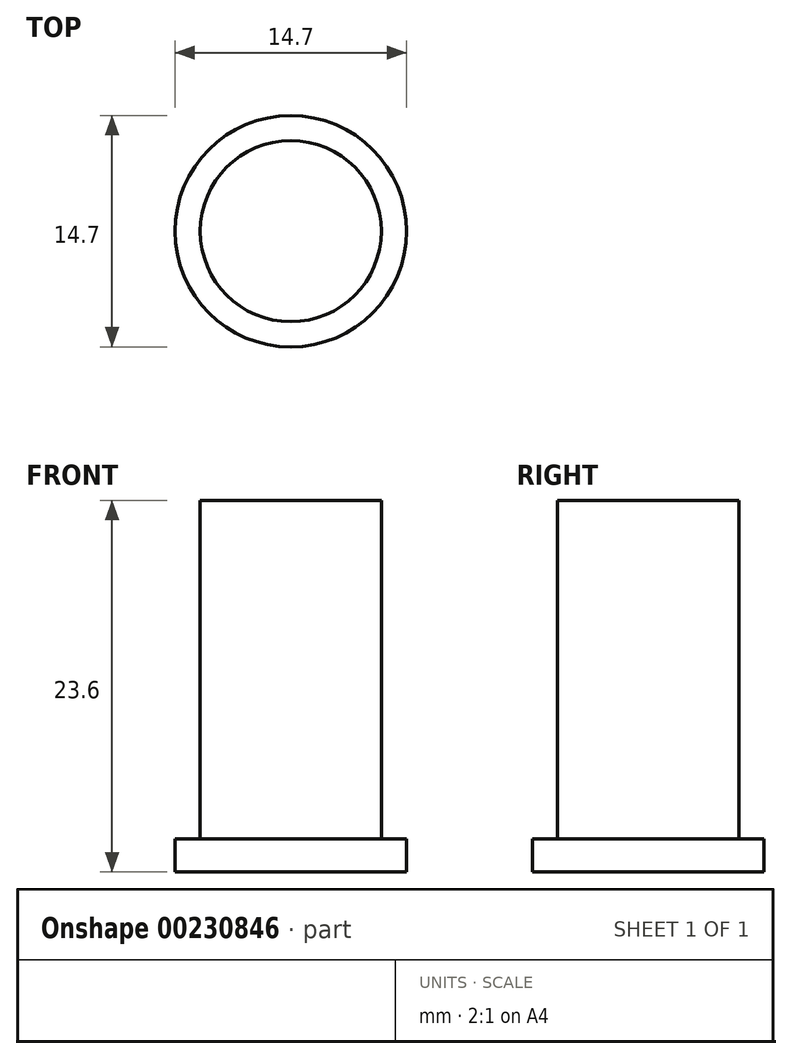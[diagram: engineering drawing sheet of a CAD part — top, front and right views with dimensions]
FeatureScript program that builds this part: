
annotation { "Feature Type Name" : "Feature", "Feature Type Description" : "" }
export const myFeature = defineFeature(function(context is Context, id is Id, definition is map)
    precondition{}
    {
        {
            var Q0;
            Q0=qCreatedBy(makeId("Top.planeOp"),FACE);
            var sketch = newSketch(context, id + "F0", { "sketchPlane" : qUnion([Q0])});
            skCircle(sketch, "E0", {"center": v(0, 0) * mm, "radius": 5.75 * mm});
            skSolve(sketch);
        }
        {
            var Q0;
            Q0=makeQuery(id+"F0.imprint","IMPRINT",FACE,{"disambiguationData":[TD([[makeQuery(id+"F0.imprint","IMPRINT",EDGE,{"derivedFrom":sQuery(id+"F0.wireOp",EDGE,"E0")}),1.0]])]});
            extrude(context, id + "F1", {"entities" : qUnion([Q0]), "depth" : 21.5 * mm});
        }
        {
            var Q0;
            Q0=makeQuery(id+"F1.opExtrude","CAP_FACE",FACE,{"disambiguationData":[OSD([sQuery(id+"F0.wireOp",EDGE,"E0")])],"isStart":true});
            var sketch = newSketch(context, id + "F2", { "sketchPlane" : qUnion([Q0])});
            skCircle(sketch, "E1", {"center": v(0, 0) * mm, "radius": 7.35 * mm});
            skSolve(sketch);
        }
        {
            var Q0;
            Q0=makeQuery(id+"F2.imprint","IMPRINT",FACE,{"disambiguationData":[TD([[makeQuery(id+"F2.imprint","IMPRINT",EDGE,{"derivedFrom":sQuery(id+"F2.wireOp",EDGE,"E1")}),1.0]])]});
            var Q1;
            Q1=makeQuery(id+"F2.imprint","IMPRINT",FACE,{"disambiguationData":[TD([[makeQuery(id+"F2.imprint","IMPRINT",EDGE,{"derivedFrom":makeQuery(id+"F1.opExtrude","CAP_EDGE",EDGE,{"disambiguationData":[OSD([sQuery(id+"F0.wireOp",EDGE,"E0")])],"isStart":true})}),-1.0]])]});
            extrude(context, id + "F3", {"entities" : qUnion([Q0, Q1]), "operationType" : NewBodyOperationType.ADD, "depth" : 2.1 * mm});
        }
    });
